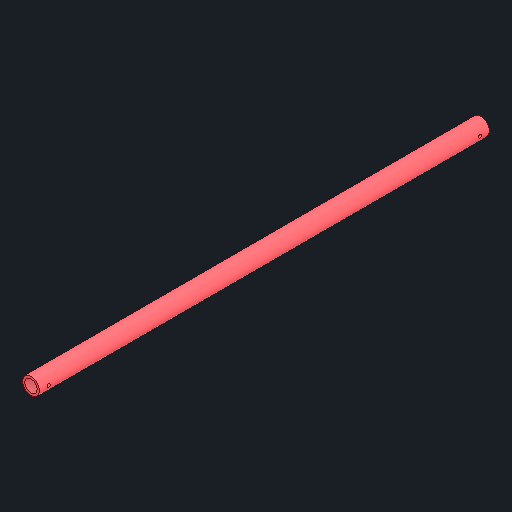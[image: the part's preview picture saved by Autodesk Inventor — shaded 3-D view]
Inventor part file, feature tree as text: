
AUTODESK INVENTOR PART (.ipt)
format: ipt  version: 2024 (Build 280153000, 153)  size: 101,888 bytes
history: native  units: in
note: dims shown in document units (in); Inventor stores cm internally (conversion verified against a paired STEP export)
features: mirror x1
ambient origin geometry x8: Origin, YZ Plane, XZ Plane, XY Plane, X Axis, Y Axis, Z Axis, Center Point
bodies: Solid1 (feature_tree)
feature tree (1):
  mirror  "Mirror1"
